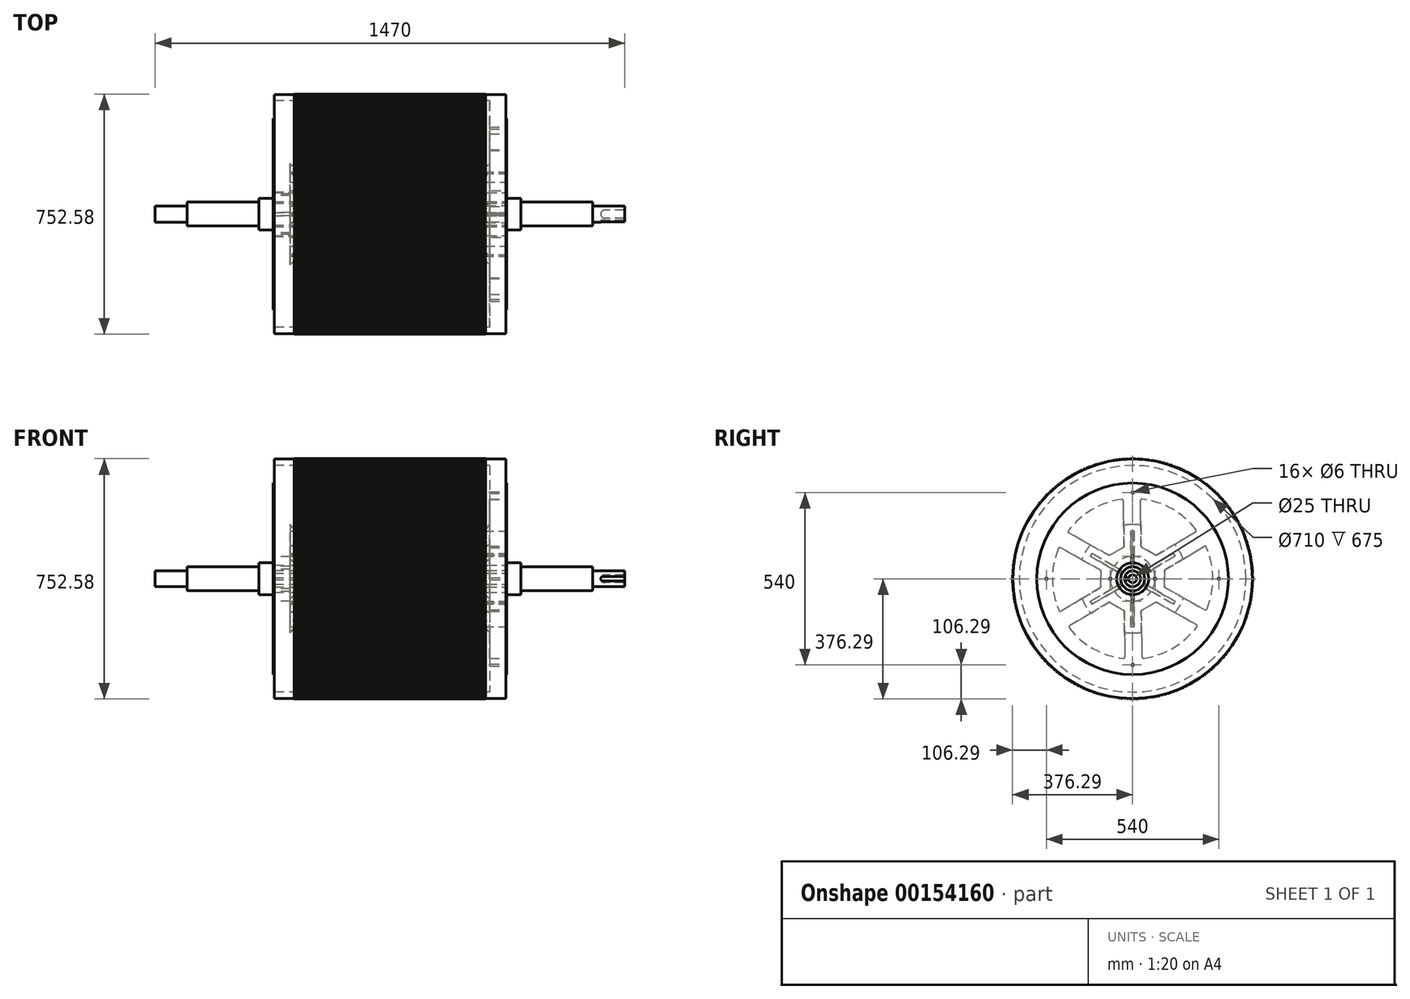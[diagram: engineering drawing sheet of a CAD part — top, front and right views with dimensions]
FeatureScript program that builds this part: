
annotation { "Feature Type Name" : "Feature", "Feature Type Description" : "" }
export const myFeature = defineFeature(function(context is Context, id is Id, definition is map)
    precondition{}
    {
        {
            var Q0;
            Q0=qCreatedBy(makeId("Front.planeOp"),FACE);
            var sketch = newSketch(context, id + "F0", { "sketchPlane" : qUnion([Q0])});
            skLineSegment(sketch, "E0", {"start": v(-128.4, 0) * mm, "end": v(171.6, 0) * mm, "construction": true});
            skLineSegment(sketch, "E1", {"start": v(0, 0) * mm, "end": v(362.5, 0) * mm});
            skLineSegment(sketch, "E2", {"start": v(0, 0) * mm, "end": v(-362.5, 0) * mm});
            skLineSegment(sketch, "E3", {"start": v(-362.5, 0) * mm, "end": v(-362.5, 375) * mm});
            skLineSegment(sketch, "E4", {"start": v(362.5, 375) * mm, "end": v(362.5, 0) * mm});
            skLineSegment(sketch, "E5.0", {"start": v(312.5, 355) * mm, "end": v(312.5, 70) * mm});
            skLineSegment(sketch, "E6", {"start": v(-312.5, 0) * mm, "end": v(-362.5, 0) * mm});
            skLineSegment(sketch, "E7", {"start": v(-362.5, 0) * mm, "end": v(-212.5, 0) * mm});
            skLineSegment(sketch, "E8", {"start": v(-212.5, 0) * mm, "end": v(-212.5, 70) * mm});
            skLineSegment(sketch, "E9", {"start": v(-212.5, 70) * mm, "end": v(-362.5, 70) * mm});
            skLineSegment(sketch, "E10.0", {"start": v(-212.5, 50) * mm, "end": v(-362.5, 50) * mm});
            skLineSegment(sketch, "E11", {"start": v(-362.5, 70) * mm, "end": v(-362.5, 50) * mm});
            skLineSegment(sketch, "E12", {"start": v(-212.5, 70) * mm, "end": v(-212.5, 50) * mm});
            skLineSegment(sketch, "E13", {"start": v(0, -51.64) * mm, "end": v(0, 29.66) * mm, "construction": true});
            skLineSegment(sketch, "E14", {"start": v(362.5, 0) * mm, "end": v(312.5, 0) * mm});
            skLineSegment(sketch, "E15", {"start": v(362.5, 0) * mm, "end": v(212.5, 0) * mm});
            skLineSegment(sketch, "E16", {"start": v(212.5, 0) * mm, "end": v(212.5, 70) * mm});
            skLineSegment(sketch, "E17", {"start": v(212.5, 70) * mm, "end": v(362.5, 70) * mm});
            skLineSegment(sketch, "E18.0", {"start": v(212.5, 50) * mm, "end": v(362.5, 50) * mm});
            skLineSegment(sketch, "E19", {"start": v(362.5, 70) * mm, "end": v(362.5, 50) * mm});
            skPoint(sketch, "E20", {"position": v(222.5, 170) * mm});
            skLineSegment(sketch, "E21", {"start": v(222.5, 170) * mm, "end": v(312.5, 170) * mm, "construction": true});
            skLineSegment(sketch, "E22", {"start": v(222.5, 170) * mm, "end": v(222.5, 70) * mm, "construction": true});
            skLineSegment(sketch, "E23", {"start": v(222.5, 70) * mm, "end": v(312.5, 170) * mm});
            skLineSegment(sketch, "E24.trimOffspring", {"start": v(-312.5, 70) * mm, "end": v(-312.5, 355) * mm});
            skPoint(sketch, "E25", {"position": v(-222.5, 170) * mm});
            skLineSegment(sketch, "E26", {"start": v(-222.5, 170) * mm, "end": v(-222.5, 70) * mm, "construction": true});
            skLineSegment(sketch, "E27", {"start": v(-222.5, 170) * mm, "end": v(-312.5, 170) * mm, "construction": true});
            skLineSegment(sketch, "E28", {"start": v(-222.5, 70) * mm, "end": v(-312.5, 170) * mm});
            skLineSegment(sketch, "E29", {"start": v(-362.5, 50) * mm, "end": v(-410, 50) * mm});
            skLineSegment(sketch, "E30", {"start": v(-410, 50) * mm, "end": v(-410, 42.5) * mm});
            skLineSegment(sketch, "E31", {"start": v(-410, 50) * mm, "end": v(-240, 50) * mm});
            skLineSegment(sketch, "E32", {"start": v(-240, 50) * mm, "end": v(-240, 0) * mm});
            skLineSegment(sketch, "E33", {"start": v(-410, 0) * mm, "end": v(-635, 0) * mm});
            skLineSegment(sketch, "E34", {"start": v(-362.5, 0) * mm, "end": v(-410, 0) * mm});
            skLineSegment(sketch, "E35", {"start": v(-635, 30) * mm, "end": v(-635, 37.5) * mm});
            skLineSegment(sketch, "E36", {"start": v(-635, 37.5) * mm, "end": v(-415, 37.5) * mm});
            skPoint(sketch, "E37.visualSharp", {"position": v(-410, 37.5) * mm});
            skArc(sketch, "E37.filletArc", {"start": v(-415, 37.5) * mm, "mid": v(-411.46, 38.96) * mm, "end": v(-410, 42.5) * mm});
            skLineSegment(sketch, "E38", {"start": v(362.5, 50) * mm, "end": v(410, 50) * mm});
            skLineSegment(sketch, "E39", {"start": v(410, 50) * mm, "end": v(410, 42.5) * mm});
            skLineSegment(sketch, "E40", {"start": v(410, 0) * mm, "end": v(362.5, 0) * mm});
            skLineSegment(sketch, "E41", {"start": v(410, 0) * mm, "end": v(635, 0) * mm});
            skLineSegment(sketch, "E42", {"start": v(635, 30) * mm, "end": v(635, 37.5) * mm});
            skLineSegment(sketch, "E43", {"start": v(635, 37.5) * mm, "end": v(415, 37.5) * mm});
            skPoint(sketch, "E44.visualSharp", {"position": v(410, 37.5) * mm});
            skArc(sketch, "E44.filletArc", {"start": v(410, 42.5) * mm, "mid": v(411.46, 38.96) * mm, "end": v(415, 37.5) * mm});
            skLineSegment(sketch, "E45", {"start": v(635, 0) * mm, "end": v(735, 0) * mm});
            skLineSegment(sketch, "E46", {"start": v(735, 0) * mm, "end": v(735, 25) * mm});
            skLineSegment(sketch, "E47", {"start": v(735, 25) * mm, "end": v(640, 25) * mm});
            skPoint(sketch, "E48.visualSharp", {"position": v(635, 25) * mm});
            skArc(sketch, "E48.filletArc", {"start": v(635, 30) * mm, "mid": v(636.46, 26.46) * mm, "end": v(640, 25) * mm});
            skLineSegment(sketch, "E49", {"start": v(735, 0) * mm, "end": v(660, 0) * mm});
            skLineSegment(sketch, "E50", {"start": v(660, 0) * mm, "end": v(660, 0) * mm});
            skLineSegment(sketch, "E51", {"start": v(672.5, 12.5) * mm, "end": v(735, 12.5) * mm});
            skPoint(sketch, "E52.visualSharp", {"position": v(660, 12.5) * mm});
            skArc(sketch, "E52.filletArc", {"start": v(672.5, 12.5) * mm, "mid": v(663.66, 8.84) * mm, "end": v(660, 0) * mm});
            skLineSegment(sketch, "E53", {"start": v(-662.73, 0) * mm, "end": v(974.4, 0) * mm, "construction": true});
            skLineSegment(sketch, "E54", {"start": v(-362.5, 50) * mm, "end": v(-362.5, 300) * mm});
            skLineSegment(sketch, "E55", {"start": v(-362.5, 300) * mm, "end": v(-365.5, 300) * mm});
            skLineSegment(sketch, "E56", {"start": v(-365.5, 300) * mm, "end": v(-365.5, 50) * mm});
            skLineSegment(sketch, "E57", {"start": v(362.5, 50) * mm, "end": v(362.5, 300) * mm});
            skLineSegment(sketch, "E58", {"start": v(362.5, 300) * mm, "end": v(365.5, 300) * mm});
            skLineSegment(sketch, "E59", {"start": v(365.5, 300) * mm, "end": v(365.5, 50) * mm});
            skLineSegment(sketch, "E60", {"start": v(-362.5, 375) * mm, "end": v(362.5, 375) * mm});
            skLineSegment(sketch, "E61.0", {"start": v(-362.5, 355) * mm, "end": v(362.5, 355) * mm});
            skLineSegment(sketch, "E62", {"start": v(-635, 0) * mm, "end": v(-735, 0) * mm});
            skLineSegment(sketch, "E63", {"start": v(-735, 0) * mm, "end": v(-735, 25) * mm});
            skLineSegment(sketch, "E64", {"start": v(-735, 25) * mm, "end": v(-640, 25) * mm});
            skPoint(sketch, "E65.visualSharp", {"position": v(-635, 25) * mm});
            skArc(sketch, "E65.filletArc", {"start": v(-640, 25) * mm, "mid": v(-636.46, 26.46) * mm, "end": v(-635, 30) * mm});
            skSolve(sketch);
        }
        {
            var Q0;
            {var subQ5=sQuery(id+"F0.wireOp",EDGE,"TOyetHQN-dl0P-lQ5R-2WxB-had5QtC8ClW3");Q0=makeQuery(id+"F0.imprint","IMPRINT",FACE,{"disambiguationData":[TD([[makeQuery(id+"F0.imprint","IMPRINT",EDGE,{"derivedFrom":subQ5}),-1.0]])]});}
            var Q1;
            {var subQ1=sQuery(id+"F0.wireOp",EDGE,"E3");var subQ5=sQuery(id+"F0.wireOp",EDGE,"547ede1c-4ac3-4899-8570-f1bddb490a53.0");var subQ6=makeQuery(id+"F0.imprint","INTERSECT",VERTEX,{"derivedFrom":[subQ1,subQ5]});Q1=makeQuery(id+"F0.imprint","IMPRINT",FACE,{"disambiguationData":[TD([[makeQuery(id+"F0.imprint","IMPRINT",EDGE,{"disambiguationData":[TD([[subQ6,-1.0]])],"derivedFrom":subQ5}),-1.0]])]});}
            var Q2;
            {var subQ4=sQuery(id+"F0.wireOp",EDGE,"547ede1c-4ac3-4899-8570-f1bddb490a53.0");var subQ6=sQuery(id+"F0.wireOp",EDGE,"E4");var subQ7=makeQuery(id+"F0.imprint","INTERSECT",VERTEX,{"derivedFrom":[subQ6,subQ4]});Q2=makeQuery(id+"F0.imprint","IMPRINT",FACE,{"disambiguationData":[TD([[makeQuery(id+"F0.imprint","IMPRINT",EDGE,{"disambiguationData":[TD([[subQ7,1.0]])],"derivedFrom":subQ4}),-1.0]])]});}
            var Q3;
            {var subQ3=sQuery(id+"F0.wireOp",EDGE,"E23");Q3=makeQuery(id+"F0.imprint","IMPRINT",FACE,{"disambiguationData":[TD([[makeQuery(id+"F0.imprint","IMPRINT",EDGE,{"derivedFrom":subQ3}),-1.0]])]});}
            var Q4;
            {var subQ6=sQuery(id+"F0.wireOp",EDGE,"E18.0");Q4=makeQuery(id+"F0.imprint","IMPRINT",FACE,{"disambiguationData":[TD([[makeQuery(id+"F0.imprint","IMPRINT",EDGE,{"derivedFrom":subQ6}),1.0]])]});}
            var Q5;
            {var subQ3=sQuery(id+"F0.wireOp",EDGE,"E18.0");Q5=makeQuery(id+"F0.imprint","IMPRINT",FACE,{"disambiguationData":[TD([[makeQuery(id+"F0.imprint","IMPRINT",EDGE,{"derivedFrom":subQ3}),-1.0]])]});}
            var Q6;
            {var subQ5=sQuery(id+"F0.wireOp",EDGE,"E32");Q6=makeQuery(id+"F0.imprint","IMPRINT",FACE,{"disambiguationData":[TD([[makeQuery(id+"F0.imprint","IMPRINT",EDGE,{"derivedFrom":subQ5}),-1.0]])]});}
            var Q7;
            {var subQ0=sQuery(id+"F0.wireOp",EDGE,"E10.0");Q7=makeQuery(id+"F0.imprint","IMPRINT",FACE,{"disambiguationData":[TD([[makeQuery(id+"F0.imprint","IMPRINT",EDGE,{"derivedFrom":subQ0}),-1.0]])]});}
            var Q8;
            {var subQ3=sQuery(id+"F0.wireOp",EDGE,"E30");Q8=makeQuery(id+"F0.imprint","IMPRINT",FACE,{"disambiguationData":[TD([[makeQuery(id+"F0.imprint","IMPRINT",EDGE,{"derivedFrom":subQ3}),1.0]])]});}
            var Q9;
            {var subQ3=sQuery(id+"F0.wireOp",EDGE,"E28");Q9=makeQuery(id+"F0.imprint","IMPRINT",FACE,{"disambiguationData":[TD([[makeQuery(id+"F0.imprint","IMPRINT",EDGE,{"derivedFrom":subQ3}),1.0]])]});}
            var Q10;
            {var subQ0=sQuery(id+"F0.wireOp",EDGE,"E38");Q10=makeQuery(id+"F0.imprint","IMPRINT",FACE,{"disambiguationData":[TD([[makeQuery(id+"F0.imprint","IMPRINT",EDGE,{"derivedFrom":subQ0}),-1.0]])]});}
            var Q11;
            {var subQ0=sQuery(id+"F0.wireOp",EDGE,"E49");Q11=makeQuery(id+"F0.imprint","IMPRINT",FACE,{"disambiguationData":[TD([[makeQuery(id+"F0.imprint","IMPRINT",EDGE,{"derivedFrom":subQ0}),-1.0]])]});}
            var Q12;
            {var subQ0=sQuery(id+"F0.wireOp",EDGE,"E58");Q12=makeQuery(id+"F0.imprint","IMPRINT",FACE,{"disambiguationData":[TD([[makeQuery(id+"F0.imprint","IMPRINT",EDGE,{"derivedFrom":subQ0}),-1.0]])]});}
            var Q13;
            {var subQ0=sQuery(id+"F0.wireOp",EDGE,"E55");Q13=makeQuery(id+"F0.imprint","IMPRINT",FACE,{"disambiguationData":[TD([[makeQuery(id+"F0.imprint","IMPRINT",EDGE,{"derivedFrom":subQ0}),1.0]])]});}
            var Q14;
            {var subQ0=sQuery(id+"F0.wireOp",EDGE,"6H8Kaumb-S9yb-812M-hJch-us6e6a0yquAi");Q14=makeQuery(id+"F0.imprint","IMPRINT",FACE,{"disambiguationData":[TD([[makeQuery(id+"F0.imprint","IMPRINT",EDGE,{"derivedFrom":subQ0}),1.0]])]});}
            var Q15;
            {var subQ1=sQuery(id+"F0.wireOp",EDGE,"E9");var subQ4=sQuery(id+"F0.wireOp",EDGE,"E54");var subQ5=makeQuery(id+"F0.imprint","INTERSECT",VERTEX,{"derivedFrom":[subQ1,subQ4]});Q15=makeQuery(id+"F0.imprint","IMPRINT",FACE,{"disambiguationData":[TD([[makeQuery(id+"F0.imprint","IMPRINT",EDGE,{"disambiguationData":[TD([[subQ5,1.0]])],"derivedFrom":subQ1}),-1.0]])]});}
            var Q16;
            {var subQ0=sQuery(id+"F0.wireOp",EDGE,"E60");Q16=makeQuery(id+"F0.imprint","IMPRINT",FACE,{"disambiguationData":[TD([[makeQuery(id+"F0.imprint","IMPRINT",EDGE,{"derivedFrom":subQ0}),-1.0]])]});}
            var Q17;
            {var subQ1=sQuery(id+"F0.wireOp",EDGE,"E5.0");var subQ8=sQuery(id+"F0.wireOp",EDGE,"E61.0");var subQ9=makeQuery(id+"F0.imprint","INTERSECT",VERTEX,{"derivedFrom":[subQ1,subQ8]});Q17=makeQuery(id+"F0.imprint","IMPRINT",FACE,{"disambiguationData":[TD([[makeQuery(id+"F0.imprint","IMPRINT",EDGE,{"disambiguationData":[TD([[subQ9,-1.0]])],"derivedFrom":subQ1}),1.0]])]});}
            var Q18;
            Q18=sQuery(id+"F0.wireOp",EDGE,"E53");
            revolve(context, id + "F1", {"entities" : qUnion([Q0, Q1, Q2, Q3, Q4, Q5, Q6, Q7, Q8, Q9, Q10, Q11, Q12, Q13, Q14, Q15, Q16, Q17]), "axis" : qUnion([Q18]), "revolveType" : RevolveType.FULL});
        }
        {
            var Q0;
            Q0=qCreatedBy(makeId("Right.planeOp"),FACE);
            cPlane(context, id + "F2", {"entities" : qUnion([Q0]), "cplaneType" : CPlaneType.OFFSET, "offset" : 362.5 * mm, "width" : 150 * mm, "height" : 150 * mm});
        }
        {
            var Q0;
            Q0=qCreatedBy(id+"F2.planeOp",FACE);
            var sketch = newSketch(context, id + "F3", { "sketchPlane" : qUnion([Q0])});
            skLineSegment(sketch, "E66", {"start": v(0, 0) * mm, "end": v(100, 0) * mm});
            skLineSegment(sketch, "E67", {"start": v(100, 0) * mm, "end": v(100, 24.17) * mm});
            skLineSegment(sketch, "E68", {"start": v(100, 0) * mm, "end": v(100, -24.06) * mm});
            skLineSegment(sketch, "E69", {"start": v(102.43, 28.46) * mm, "end": v(223.77, 101.26) * mm});
            skLineSegment(sketch, "E70", {"start": v(102.57, -28.43) * mm, "end": v(225.8, -96.84) * mm});
            skArc(sketch, "E71", {"start": v(230.94, 98.94) * mm, "mid": v(251.23, 2.49) * mm, "end": v(232.85, -94.34) * mm});
            skPoint(sketch, "E72.visualSharp", {"position": v(228.63, 104.17) * mm});
            skArc(sketch, "E72.filletArc", {"start": v(230.94, 98.94) * mm, "mid": v(227.88, 101.73) * mm, "end": v(223.77, 101.26) * mm});
            skPoint(sketch, "E73.newPointA", {"position": v(231.14, -99.8) * mm});
            skArc(sketch, "E73.filletArc", {"start": v(225.8, -96.84) * mm, "mid": v(229.88, -97.18) * mm, "end": v(232.85, -94.34) * mm});
            skPoint(sketch, "E74.visualSharp", {"position": v(100, 27) * mm});
            skArc(sketch, "E74.filletArc", {"start": v(102.43, 28.46) * mm, "mid": v(100.65, 26.63) * mm, "end": v(100, 24.17) * mm});
            skPoint(sketch, "E75.visualSharp", {"position": v(100, -27) * mm});
            skArc(sketch, "E75.filletArc", {"start": v(100, -24.06) * mm, "mid": v(100.7, -26.6) * mm, "end": v(102.57, -28.43) * mm});
            skArc(sketch, "E76.1.0", {"start": v(29.79, 249.47) * mm, "mid": v(123.46, 218.81) * mm, "end": v(198.13, 154.48) * mm});
            skArc(sketch, "E76.1.1", {"start": v(29.79, 249.47) * mm, "mid": v(25.84, 248.21) * mm, "end": v(24.2, 244.42) * mm});
            skLineSegment(sketch, "E76.1.2", {"start": v(26.57, 102.93) * mm, "end": v(24.2, 244.42) * mm});
            skLineSegment(sketch, "E76.1.3", {"start": v(50, 86.6) * mm, "end": v(29.07, 98.69) * mm});
            skArc(sketch, "E76.1.4", {"start": v(26.57, 102.93) * mm, "mid": v(27.26, 100.48) * mm, "end": v(29.07, 98.69) * mm});
            skLineSegment(sketch, "E76.1.5", {"start": v(50, 86.6) * mm, "end": v(70.83, 74.57) * mm});
            skArc(sketch, "E76.1.6", {"start": v(70.83, 74.57) * mm, "mid": v(73.38, 73.9) * mm, "end": v(75.9, 74.62) * mm});
            skLineSegment(sketch, "E76.1.7", {"start": v(75.9, 74.62) * mm, "end": v(196.76, 147.12) * mm});
            skArc(sketch, "E76.1.8", {"start": v(196.76, 147.12) * mm, "mid": v(199.1, 150.5) * mm, "end": v(198.13, 154.48) * mm});
            skArc(sketch, "E76.2.0", {"start": v(-201.15, 150.53) * mm, "mid": v(-127.77, 216.33) * mm, "end": v(-34.72, 248.83) * mm});
            skArc(sketch, "E76.2.1", {"start": v(-201.15, 150.53) * mm, "mid": v(-202.04, 146.49) * mm, "end": v(-199.58, 143.16) * mm});
            skLineSegment(sketch, "E76.2.2", {"start": v(-75.86, 74.48) * mm, "end": v(-199.58, 143.16) * mm});
            skLineSegment(sketch, "E76.2.3", {"start": v(-50, 86.6) * mm, "end": v(-70.93, 74.52) * mm});
            skArc(sketch, "E76.2.4", {"start": v(-75.86, 74.48) * mm, "mid": v(-73.39, 73.85) * mm, "end": v(-70.93, 74.52) * mm});
            skLineSegment(sketch, "E76.2.5", {"start": v(-50, 86.6) * mm, "end": v(-29.17, 98.63) * mm});
            skArc(sketch, "E76.2.6", {"start": v(-29.17, 98.63) * mm, "mid": v(-27.32, 100.5) * mm, "end": v(-26.67, 103.05) * mm});
            skLineSegment(sketch, "E76.2.7", {"start": v(-26.67, 103.05) * mm, "end": v(-29.03, 243.96) * mm});
            skArc(sketch, "E76.2.8", {"start": v(-29.03, 243.96) * mm, "mid": v(-30.78, 247.68) * mm, "end": v(-34.72, 248.83) * mm});
            skArc(sketch, "E76.3.0", {"start": v(-230.94, -98.94) * mm, "mid": v(-251.23, -2.49) * mm, "end": v(-232.85, 94.34) * mm});
            skArc(sketch, "E76.3.1", {"start": v(-230.94, -98.94) * mm, "mid": v(-227.88, -101.73) * mm, "end": v(-223.77, -101.26) * mm});
            skLineSegment(sketch, "E76.3.2", {"start": v(-102.43, -28.46) * mm, "end": v(-223.77, -101.26) * mm});
            skLineSegment(sketch, "E76.3.3", {"start": v(-100, 0) * mm, "end": v(-100, -24.17) * mm});
            skArc(sketch, "E76.3.4", {"start": v(-102.43, -28.46) * mm, "mid": v(-100.65, -26.63) * mm, "end": v(-100, -24.17) * mm});
            skLineSegment(sketch, "E76.3.5", {"start": v(-100, 0) * mm, "end": v(-100, 24.06) * mm});
            skArc(sketch, "E76.3.6", {"start": v(-100, 24.06) * mm, "mid": v(-100.7, 26.6) * mm, "end": v(-102.57, 28.43) * mm});
            skLineSegment(sketch, "E76.3.7", {"start": v(-102.57, 28.43) * mm, "end": v(-225.8, 96.84) * mm});
            skArc(sketch, "E76.3.8", {"start": v(-225.8, 96.84) * mm, "mid": v(-229.88, 97.18) * mm, "end": v(-232.85, 94.34) * mm});
            skArc(sketch, "E76.4.0", {"start": v(-29.79, -249.47) * mm, "mid": v(-123.46, -218.81) * mm, "end": v(-198.13, -154.48) * mm});
            skArc(sketch, "E76.4.1", {"start": v(-29.79, -249.47) * mm, "mid": v(-25.84, -248.21) * mm, "end": v(-24.2, -244.42) * mm});
            skLineSegment(sketch, "E76.4.2", {"start": v(-26.57, -102.93) * mm, "end": v(-24.2, -244.42) * mm});
            skLineSegment(sketch, "E76.4.3", {"start": v(-50, -86.6) * mm, "end": v(-29.07, -98.69) * mm});
            skArc(sketch, "E76.4.4", {"start": v(-26.57, -102.93) * mm, "mid": v(-27.26, -100.48) * mm, "end": v(-29.07, -98.69) * mm});
            skLineSegment(sketch, "E76.4.5", {"start": v(-50, -86.6) * mm, "end": v(-70.83, -74.57) * mm});
            skArc(sketch, "E76.4.6", {"start": v(-70.83, -74.57) * mm, "mid": v(-73.38, -73.9) * mm, "end": v(-75.9, -74.62) * mm});
            skLineSegment(sketch, "E76.4.7", {"start": v(-75.9, -74.62) * mm, "end": v(-196.76, -147.12) * mm});
            skArc(sketch, "E76.4.8", {"start": v(-196.76, -147.12) * mm, "mid": v(-199.1, -150.5) * mm, "end": v(-198.13, -154.48) * mm});
            skArc(sketch, "E76.5.0", {"start": v(201.15, -150.53) * mm, "mid": v(127.77, -216.33) * mm, "end": v(34.72, -248.83) * mm});
            skArc(sketch, "E76.5.1", {"start": v(201.15, -150.53) * mm, "mid": v(202.04, -146.49) * mm, "end": v(199.58, -143.16) * mm});
            skLineSegment(sketch, "E76.5.2", {"start": v(75.86, -74.48) * mm, "end": v(199.58, -143.16) * mm});
            skLineSegment(sketch, "E76.5.3", {"start": v(50, -86.6) * mm, "end": v(70.93, -74.52) * mm});
            skArc(sketch, "E76.5.4", {"start": v(75.86, -74.48) * mm, "mid": v(73.39, -73.85) * mm, "end": v(70.93, -74.52) * mm});
            skLineSegment(sketch, "E76.5.5", {"start": v(50, -86.6) * mm, "end": v(29.17, -98.63) * mm});
            skArc(sketch, "E76.5.6", {"start": v(29.17, -98.63) * mm, "mid": v(27.32, -100.5) * mm, "end": v(26.67, -103.05) * mm});
            skLineSegment(sketch, "E76.5.7", {"start": v(26.67, -103.05) * mm, "end": v(29.03, -243.96) * mm});
            skArc(sketch, "E76.5.8", {"start": v(29.03, -243.96) * mm, "mid": v(30.78, -247.68) * mm, "end": v(34.72, -248.83) * mm});
            skLineSegment(sketch, "E77", {"start": v(0, 0) * mm, "end": v(0, 150) * mm});
            skLineSegment(sketch, "E78", {"start": v(0, 150) * mm, "end": v(-5, 149.92) * mm});
            skLineSegment(sketch, "E79", {"start": v(0, 150) * mm, "end": v(5, 149.96) * mm});
            skPoint(sketch, "E79.endSnap0", {"position": v(-2.5, 149.96) * mm});
            skLineSegment(sketch, "E80", {"start": v(0, 0) * mm, "end": v(0, 42.5) * mm});
            skLineSegment(sketch, "E81", {"start": v(5, 149.96) * mm, "end": v(5, 42.5) * mm});
            skLineSegment(sketch, "E82", {"start": v(5, 42.5) * mm, "end": v(-5, 42.5) * mm});
            skLineSegment(sketch, "E83", {"start": v(-5, 42.5) * mm, "end": v(-5, 149.92) * mm});
            skLineSegment(sketch, "E84.1.0", {"start": v(-127.37, 79.3) * mm, "end": v(-34.3, 25.58) * mm});
            skLineSegment(sketch, "E84.1.1", {"start": v(-39.3, 16.92) * mm, "end": v(-132.33, 70.63) * mm});
            skLineSegment(sketch, "E84.1.2", {"start": v(-129.9, 75) * mm, "end": v(-127.37, 79.3) * mm});
            skLineSegment(sketch, "E84.1.3", {"start": v(-129.9, 75) * mm, "end": v(-132.33, 70.63) * mm});
            skLineSegment(sketch, "E84.1.4", {"start": v(-34.3, 25.58) * mm, "end": v(-39.3, 16.92) * mm});
            skLineSegment(sketch, "E84.2.0", {"start": v(-132.37, -70.65) * mm, "end": v(-39.3, -16.92) * mm});
            skLineSegment(sketch, "E84.2.1", {"start": v(-34.3, -25.58) * mm, "end": v(-127.33, -79.29) * mm});
            skLineSegment(sketch, "E84.2.2", {"start": v(-129.9, -75) * mm, "end": v(-132.37, -70.65) * mm});
            skLineSegment(sketch, "E84.2.3", {"start": v(-129.9, -75) * mm, "end": v(-127.33, -79.29) * mm});
            skLineSegment(sketch, "E84.2.4", {"start": v(-39.3, -16.92) * mm, "end": v(-34.3, -25.58) * mm});
            skLineSegment(sketch, "E84.3.0", {"start": v(-5, -149.96) * mm, "end": v(-5, -42.5) * mm});
            skLineSegment(sketch, "E84.3.1", {"start": v(5, -42.5) * mm, "end": v(5, -149.92) * mm});
            skLineSegment(sketch, "E84.3.2", {"start": v(0, -150) * mm, "end": v(-5, -149.96) * mm});
            skLineSegment(sketch, "E84.3.3", {"start": v(0, -150) * mm, "end": v(5, -149.92) * mm});
            skLineSegment(sketch, "E84.3.4", {"start": v(-5, -42.5) * mm, "end": v(5, -42.5) * mm});
            skLineSegment(sketch, "E84.4.0", {"start": v(127.37, -79.3) * mm, "end": v(34.3, -25.58) * mm});
            skLineSegment(sketch, "E84.4.1", {"start": v(39.3, -16.92) * mm, "end": v(132.33, -70.63) * mm});
            skLineSegment(sketch, "E84.4.2", {"start": v(129.9, -75) * mm, "end": v(127.37, -79.3) * mm});
            skLineSegment(sketch, "E84.4.3", {"start": v(129.9, -75) * mm, "end": v(132.33, -70.63) * mm});
            skLineSegment(sketch, "E84.4.4", {"start": v(34.3, -25.58) * mm, "end": v(39.3, -16.92) * mm});
            skLineSegment(sketch, "E84.5.0", {"start": v(132.37, 70.65) * mm, "end": v(39.3, 16.92) * mm});
            skLineSegment(sketch, "E84.5.1", {"start": v(34.3, 25.58) * mm, "end": v(127.33, 79.29) * mm});
            skLineSegment(sketch, "E84.5.2", {"start": v(129.9, 75) * mm, "end": v(132.37, 70.65) * mm});
            skLineSegment(sketch, "E84.5.3", {"start": v(129.9, 75) * mm, "end": v(127.33, 79.29) * mm});
            skLineSegment(sketch, "E84.5.4", {"start": v(39.3, 16.92) * mm, "end": v(34.3, 25.58) * mm});
            skSolve(sketch);
        }
        {
            var Q0;
            Q0 = qSketchRegion(id + "F3", true);
            extrude(context, id + "F4", {"entities" : qUnion([Q0]), "operationType" : NewBodyOperationType.REMOVE, "oppositeDirection" : true, "depth" : 725 * mm});
        }
        {
            var Q0;
            Q0=qCreatedBy(makeId("Front.planeOp"),FACE);
            cPlane(context, id + "F5", {"entities" : qUnion([Q0]), "cplaneType" : CPlaneType.OFFSET, "offset" : 25 * mm, "width" : 150 * mm, "height" : 150 * mm});
        }
        {
            var Q0;
            Q0=qCreatedBy(id+"F5.planeOp",FACE);
            var sketch = newSketch(context, id + "F6", { "sketchPlane" : qUnion([Q0])});
            skLineSegment(sketch, "E85.0", {"start": v(735, -25) * mm, "end": v(735, 25) * mm});
            skLineSegment(sketch, "E86", {"start": v(735, -25) * mm, "end": v(735, 0) * mm});
            skLineSegment(sketch, "E87", {"start": v(735, 0) * mm, "end": v(697.5, 0) * mm});
            skLineSegment(sketch, "E88.left", {"start": v(735, 7) * mm, "end": v(735, -7) * mm});
            skPoint(sketch, "E88.middle", {"position": v(697.5, 0) * mm});
            skLineSegment(sketch, "E89.bottom", {"start": v(735, 7) * mm, "end": v(667, 7) * mm});
            skLineSegment(sketch, "E89.top", {"start": v(735, -7) * mm, "end": v(667, -7) * mm});
            skLineSegment(sketch, "E89.right", {"start": v(660, 0) * mm, "end": v(660, 0) * mm});
            skPoint(sketch, "E90.visualSharp", {"position": v(660, 7) * mm});
            skArc(sketch, "E90.filletArc", {"start": v(667, 7) * mm, "mid": v(662.05, 4.95) * mm, "end": v(660, 0) * mm});
            skPoint(sketch, "E91.visualSharp", {"position": v(660, -7) * mm});
            skArc(sketch, "E91.filletArc", {"start": v(660, 0) * mm, "mid": v(662.05, -4.95) * mm, "end": v(667, -7) * mm});
            skSolve(sketch);
        }
        {
            var Q0;
            Q0 = qSketchRegion(id + "F6", true);
            extrude(context, id + "F7", {"entities" : qUnion([Q0]), "operationType" : NewBodyOperationType.REMOVE, "oppositeDirection" : true, "depth" : 6.5 * mm});
        }
        {
            var Q0;
            Q0=qCreatedBy(makeId("Right.planeOp"),FACE);
            cPlane(context, id + "F8", {"entities" : qUnion([Q0]), "cplaneType" : CPlaneType.OFFSET, "offset" : 300 * mm, "width" : 150 * mm, "height" : 150 * mm});
        }
        {
            var Q0;
            Q0=qCreatedBy(id+"F8.planeOp",FACE);
            var sketch = newSketch(context, id + "F9", { "sketchPlane" : qUnion([Q0])});
            skArc(sketch, "E92.0", {"start": v(-29.98, 373.8) * mm, "mid": v(-30.58, 373.75) * mm, "end": v(-31.18, 373.7) * mm});
            skLineSegment(sketch, "E93", {"start": v(-31.18, 373.7) * mm, "end": v(-31.18, 375) * mm});
            skLineSegment(sketch, "E94", {"start": v(-31.18, 375) * mm, "end": v(-29.98, 375) * mm});
            skLineSegment(sketch, "E95", {"start": v(-29.98, 375) * mm, "end": v(-29.98, 373.8) * mm});
            skSolve(sketch);
        }
        {
            var Q0;
            Q0 = qSketchRegion(id + "F9", true);
            extrude(context, id + "F10", {"entities" : qUnion([Q0]), "oppositeDirection" : true, "depth" : 600 * mm});
        }
        {
            var Q0;
            Q0=makeQuery(id+"F10.opExtrude","SWEPT_BODY",BODY,{"disambiguationData":[OSD([sQuery(id+"F9.wireOp",EDGE,"E92.0"),sQuery(id+"F9.wireOp",EDGE,"E93"),sQuery(id+"F9.wireOp",EDGE,"E94"),sQuery(id+"F9.wireOp",EDGE,"E95")])]});
            var Q1;
            Q1=makeQuery(id+"F1.opRevolve","SWEPT_FACE",FACE,{"disambiguationData":[OSD([sQuery(id+"F0.wireOp",EDGE,"E60")])]});
            circularPattern(context, id + "F11", {"entities" : qUnion([Q0]), "axis" : qUnion([Q1]), "angle" : 0.5 * degree, "instanceCount" : 725});
        }
        {
            var Q0;
            Q0=makeQuery(id+"F1.opRevolve","SWEPT_FACE",FACE,{"disambiguationData":[OSD([sQuery(id+"F0.wireOp",EDGE,"E59")])]});
            var sketch = newSketch(context, id + "F12", { "sketchPlane" : qUnion([Q0])});
            skLineSegment(sketch, "E96", {"start": v(0, 0) * mm, "end": v(0, 270) * mm});
            skCircle(sketch, "E97", {"center": v(0, 270) * mm, "radius": 3 * mm});
            skPoint(sketch, "E98", {"position": v(270, 0) * mm});
            skPoint(sketch, "E99", {"position": v(0, 0) * mm});
            skPoint(sketch, "E100", {"position": v(-270, 0) * mm});
            skPoint(sketch, "E101", {"position": v(0, -270) * mm});
            skCircle(sketch, "E102", {"center": v(-270, 0) * mm, "radius": 3 * mm});
            skCircle(sketch, "E103", {"center": v(270, 0) * mm, "radius": 3 * mm});
            skCircle(sketch, "E104", {"center": v(0, -270) * mm, "radius": 3 * mm});
            skPoint(sketch, "E105", {"position": v(0, -70) * mm});
            skPoint(sketch, "E106", {"position": v(0, 70) * mm});
            skPoint(sketch, "E107", {"position": v(-70, 0) * mm});
            skPoint(sketch, "E108", {"position": v(70, 0) * mm});
            skCircle(sketch, "E109", {"center": v(0, 70) * mm, "radius": 3 * mm});
            skCircle(sketch, "E110", {"center": v(-70, 0) * mm, "radius": 3 * mm});
            skCircle(sketch, "E111", {"center": v(0, -70) * mm, "radius": 3 * mm});
            skCircle(sketch, "E112", {"center": v(70, 0) * mm, "radius": 3 * mm});
            skSolve(sketch);
        }
        {
            var Q0;
            Q0 = qSketchRegion(id + "F12", true);
            extrude(context, id + "F13", {"entities" : qUnion([Q0]), "operationType" : NewBodyOperationType.REMOVE, "oppositeDirection" : true, "depth" : 731 * mm});
        }
    });
